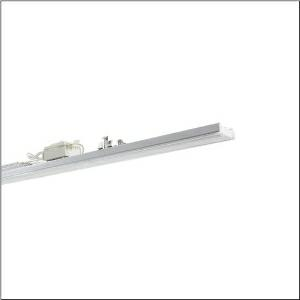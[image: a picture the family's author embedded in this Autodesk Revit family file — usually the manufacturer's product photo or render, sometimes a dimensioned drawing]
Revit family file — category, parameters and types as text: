
# Revit family: licross_r__21_recessed_mo_52te107n485g_2b82
name_source: partatom
category: Lighting Fixtures
units: mm (PartAtom-declared; Revit-internal decimal feet)

## family parameters
Cut with Voids When Loaded = No
Host = Face
Light Source = No
Part Type = Normal
Room Calculation Point = No
Round Connector Dimension = Use Diameter
Shared = No

## types (1)
- Licross® 21 Recessed MO (1 x LED, 8580 lm, 47.9 W, 4000K)
    Apparent Load = 48 VA
    CIE Flux Codes = 50 81 96 100 100
    Color Rendering = 80
    Color Temperature = 4000K
    Default Elevation = 1800 mm
    Description = Licross® 21 Recessed MO, luminaire insert, of sheet steel, galvanised, coil coated, white, length: 1.500mm, width: 66mm, height: 67mm, LED rated luminous flux: 8.560lm, light colour: 840, control gear: ON/OFF, with plug, 3-pole, with phase selection, mains connection: 220..240V, AC, 50/60Hz, rated input power: 48W, halogen-free wiring, primary optical cover: cover, of PMMA, light emission: direct distribution, primary light characteristic: symmetric, protection rating (complete): IP54, insulation class (complete): insulation class I (protective earthing), certification: CE, ENEC, VDE, UKCA, protection symbol: D if used in an environment with non-conductive dust loads with corresponding accessories, impact resistance: IK06, permissible ambient temperature for indoor applications: -35..+40°C, corresponds to IFS (International Featured Standards) requirements for safety and quality in the food industry, reducing of maximum allowable ambient temperature of 5°C with ceiling mounting, LABS conformity tested according to VDMA 24364:2018-05, packaging unit: 1 piece
    Height = 58 mm
    Lamp = 1 x LED
    Lamp Light Flux = 8580 lm
    Lamp Power = 47.9 W
    Lamp count = 1
    Length = 1500 mm
    Luminous efficacy = 179 lm/W
    Manufacturer = Siteco
    ModVariant = No
    Model = 52TE107N485G
    Mounting Place = Ceiling
    Mounting Type = Pendant
    Number of Poles = 1
    OnlyDefault = Yes
    Power Factor = 1
    Product Name = Licross® 21 Recessed MO
    Product group = luminaire insert
    ProductGroupID = 902
    Protection Class = Protection class I
    Protection Degree = IP 54
    RLX_Detail_Level = 1
    RLX_Emergency_Light_Flux = 0 lm
    RLX_Emergency_Type = 0
    RLX_Emergency_Type_DB = No
    RlxData = <blob elided: 20741 chars, md5=958fe450>
    Socket = socket
    Standby Power = 0 W
    System Light Flux = 8580 lm
    System Power = 48 W
    Type Comments = Product without accessories
    Type Image = l_1296930.jpg
    URL = http://relux.com
    VarID = ---
    Voltage = 0 V
    Weight = 0.00 kg
    Width = 66 mm

## geometry (parser evidence)
native form markers: Blend x4, Sweep x11
no freeform markers — native parametric forms only
